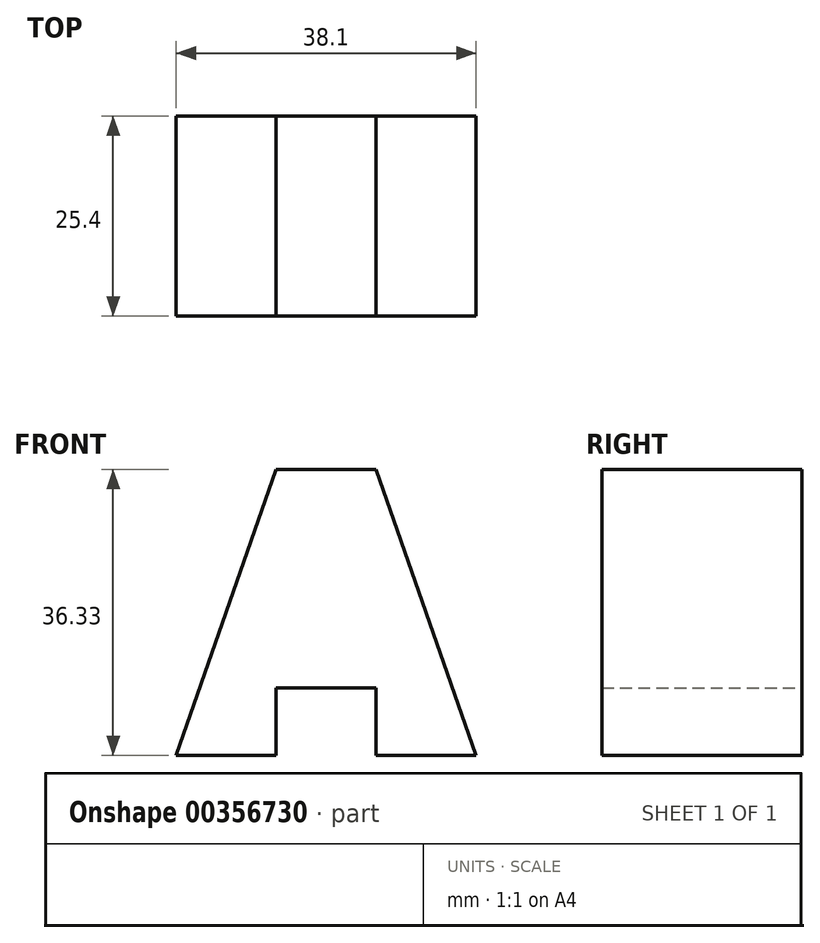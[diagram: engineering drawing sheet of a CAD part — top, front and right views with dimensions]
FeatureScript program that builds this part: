
annotation { "Feature Type Name" : "Feature", "Feature Type Description" : "" }
export const myFeature = defineFeature(function(context is Context, id is Id, definition is map)
    precondition{}
    {
        {
            var Q0;
            Q0=qCreatedBy(makeId("Front.planeOp"),FACE);
            var sketch = newSketch(context, id + "F0", { "sketchPlane" : qUnion([Q0])});
            skLineSegment(sketch, "E0", {"start": v(-52.57, 0) * mm, "end": v(-39.87, 0) * mm});
            skLineSegment(sketch, "E1", {"start": v(-39.87, 0) * mm, "end": v(-39.87, 8.57) * mm});
            skLineSegment(sketch, "E2", {"start": v(-27.17, 8.57) * mm, "end": v(-27.17, 0) * mm});
            skLineSegment(sketch, "E3", {"start": v(-27.17, 0) * mm, "end": v(-14.47, 0) * mm});
            skLineSegment(sketch, "E4", {"start": v(-27.17, 36.33) * mm, "end": v(-39.87, 36.33) * mm});
            skLineSegment(sketch, "E5", {"start": v(-39.87, 36.33) * mm, "end": v(-52.57, 0) * mm});
            skLineSegment(sketch, "E6", {"start": v(-27.17, 36.33) * mm, "end": v(-14.47, 0) * mm});
            skLineSegment(sketch, "E7", {"start": v(-39.87, 8.57) * mm, "end": v(-27.17, 8.57) * mm});
            skSolve(sketch);
        }
        {
            var Q0;
            Q0=makeQuery(id+"F0.imprint","IMPRINT",FACE,{"disambiguationData":[TD([[makeQuery(id+"F0.imprint","IMPRINT",EDGE,{"derivedFrom":sQuery(id+"F0.wireOp",EDGE,"E0")}),1.0]])]});
            extrude(context, id + "F1", {"entities" : qUnion([Q0]), "depth" : 25.4 * mm});
        }
    });
